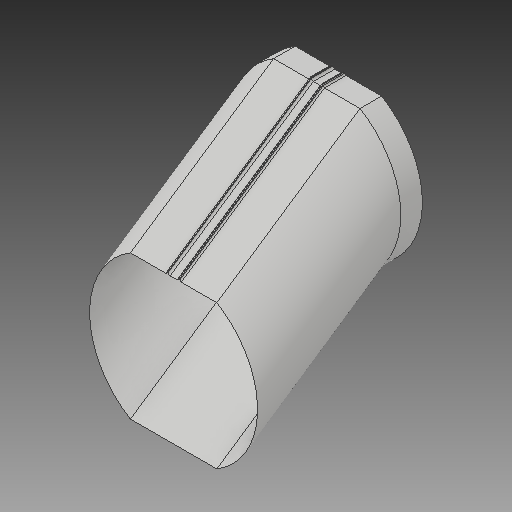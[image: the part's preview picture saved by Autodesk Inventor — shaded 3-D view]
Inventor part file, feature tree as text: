
AUTODESK INVENTOR PART (.ipt)
format: ipt  version: 2017 (Build 210142000, 142)  size: 169,984 bytes
history: native  units: in
note: dims shown in document units (in); Inventor stores cm internally (conversion verified against a paired STEP export)
features: sketch x2, extrude x1, plane x1, sweep x1, delete_face x1
ambient origin geometry x8: Origin, YZ Plane, XZ Plane, XY Plane, X Axis, Y Axis, Z Axis, Center Point
bodies: Solid1 (feature_tree)
feature tree (6):
  sketch  "Sketch1"  dims[d0=6.6667in d3=1.0in d4=0.0in d12=8.0in]
  extrude  "connecction top"  Depth=6.6667in
  plane  "Work Plane2"
  sweep  "ramp"
  delete_face  "Delete Face1"
  sketch  "Sketch6"  dims[d28=8.0in d45=0.0in d46=0.0in d65=0.8521in d66=4.0in d67=0.5833in d68=3.8873in d69=3.8873in d70=1.7083in d71=0.0625in d72=0.0625in d73=1.6458in d74=0.25in d75=0.125in d77=0.0884in d78=45.0deg d79=3.3333in d80=0.125in]
